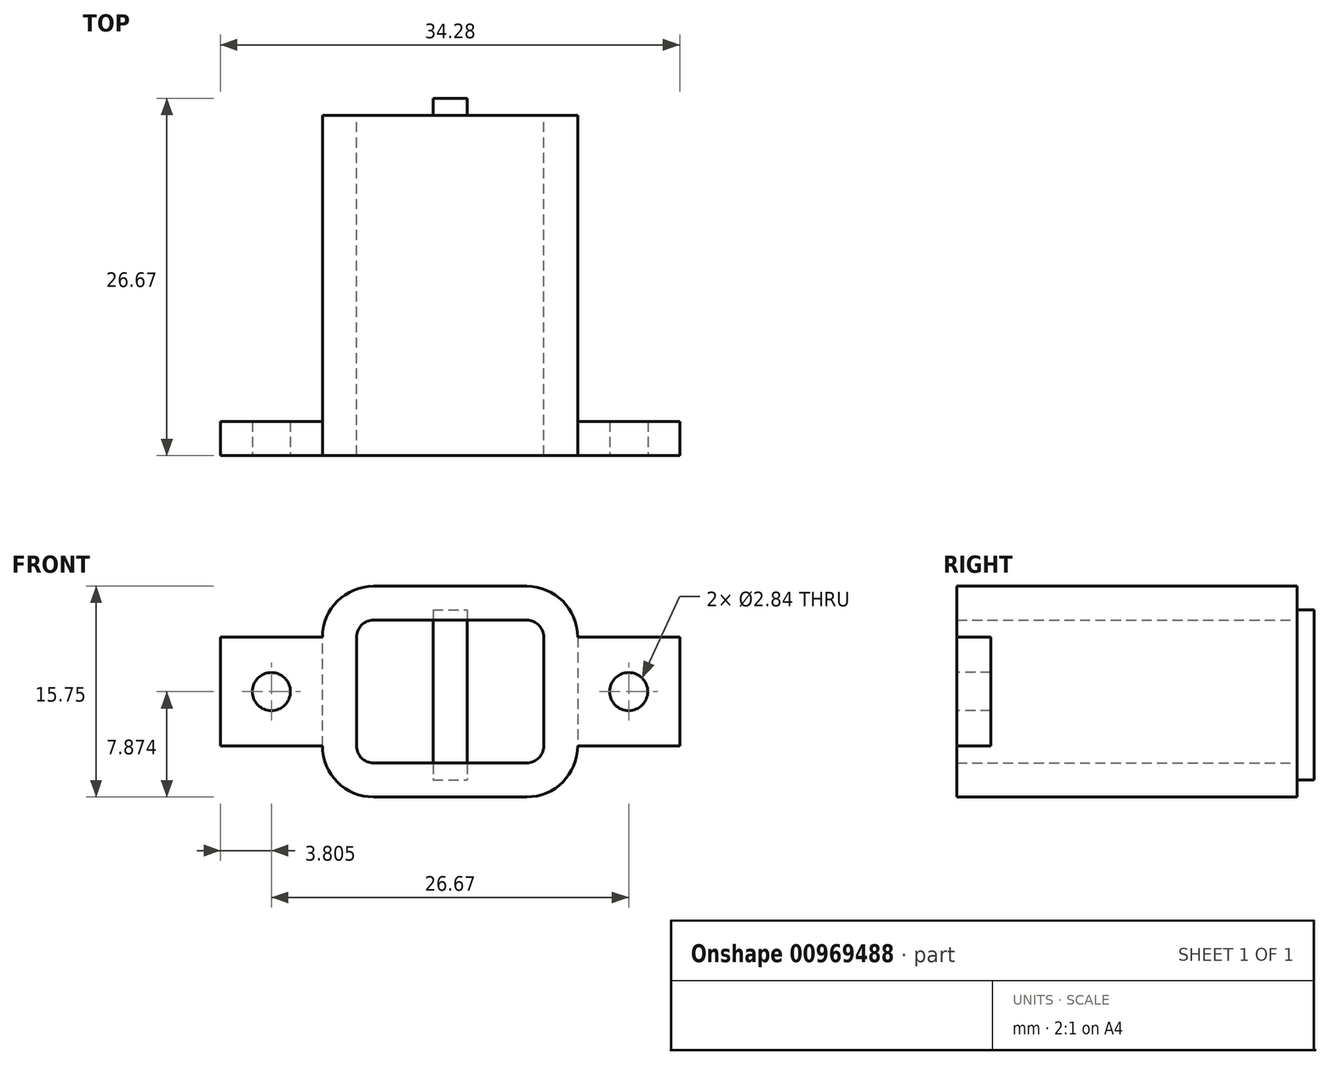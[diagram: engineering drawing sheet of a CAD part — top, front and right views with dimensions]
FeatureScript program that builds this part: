
annotation { "Feature Type Name" : "Feature", "Feature Type Description" : "" }
export const myFeature = defineFeature(function(context is Context, id is Id, definition is map)
    precondition{}
    {
        {
            var Q0;
            Q0=qCreatedBy(makeId("Front.planeOp"),FACE);
            var sketch = newSketch(context, id + "F0", { "sketchPlane" : qUnion([Q0])});
            skLineSegment(sketch, "E0", {"start": v(-6.99, 1.27) * mm, "end": v(-6.99, 9.4) * mm});
            skLineSegment(sketch, "E1", {"start": v(-5.72, 10.67) * mm, "end": v(5.72, 10.67) * mm});
            skLineSegment(sketch, "E2", {"start": v(6.99, 9.4) * mm, "end": v(6.99, 1.27) * mm});
            skPoint(sketch, "E3.visualSharp", {"position": v(-6.99, 0) * mm});
            skPoint(sketch, "E4.visualSharp", {"position": v(6.99, 0) * mm});
            skPoint(sketch, "E5.visualSharp", {"position": v(6.99, 10.67) * mm});
            skArc(sketch, "E5.filletArc", {"start": v(6.99, 9.4) * mm, "mid": v(6.61, 10.3) * mm, "end": v(5.72, 10.67) * mm});
            skPoint(sketch, "E6.visualSharp", {"position": v(-6.99, 10.67) * mm});
            skArc(sketch, "E6.filletArc", {"start": v(-5.72, 10.67) * mm, "mid": v(-6.61, 10.3) * mm, "end": v(-6.99, 9.4) * mm});
            skLineSegment(sketch, "E7", {"start": v(-5.72, 0) * mm, "end": v(5.72, 0) * mm});
            skArc(sketch, "E8.filletArc", {"start": v(-6.99, 1.27) * mm, "mid": v(-6.61, 0.37) * mm, "end": v(-5.72, 0) * mm});
            skArc(sketch, "E9.filletArc", {"start": v(5.72, 0) * mm, "mid": v(6.61, 0.37) * mm, "end": v(6.99, 1.27) * mm});
            skSolve(sketch);
        }
        {
            var Q0;
            Q0=qCreatedBy(makeId("Right.planeOp"),FACE);
            var sketch = newSketch(context, id + "F1", { "sketchPlane" : qUnion([Q0])});
            skLineSegment(sketch, "E10", {"start": v(-12.7, 13.2) * mm, "end": v(-12.7, 10.67) * mm});
            skLineSegment(sketch, "E11", {"start": v(12.7, 13.2) * mm, "end": v(12.7, 10.67) * mm});
            skLineSegment(sketch, "E12", {"start": v(12.7, 13.2) * mm, "end": v(-12.7, 13.2) * mm});
            skLineSegment(sketch, "E13", {"start": v(-12.7, 10.67) * mm, "end": v(12.7, 10.67) * mm});
            skSolve(sketch);
        }
        {
            var Q0;
            Q0 = qSketchRegion(id + "F1", true);
            var Q1;
            Q1=sQuery(id+"F0.wireOp",EDGE,"E1");
            var Q2;
            Q2=sQuery(id+"F0.wireOp",EDGE,"E6.filletArc");
            var Q3;
            Q3=sQuery(id+"F0.wireOp",EDGE,"E0");
            var Q4;
            Q4=sQuery(id+"F0.wireOp",EDGE,"E8.filletArc");
            var Q5;
            Q5=sQuery(id+"F0.wireOp",EDGE,"E7");
            var Q6;
            Q6=sQuery(id+"F0.wireOp",EDGE,"E9.filletArc");
            var Q7;
            Q7=sQuery(id+"F0.wireOp",EDGE,"E2");
            var Q8;
            Q8=sQuery(id+"F0.wireOp",EDGE,"E5.filletArc");
            sweep(context, id + "F2", {"profiles" : qUnion([Q0]), "path" : qUnion([Q1, Q2, Q3, Q4, Q5, Q6, Q7, Q8])});
        }
        {
            var Q0;
            Q0=makeQuery(id+"F2.opSweep","SWEPT_FACE",FACE,{"disambiguationData":[OSD([sQuery(id+"F0.wireOp",EDGE,"E0"),sQuery(id+"F1.wireOp",EDGE,"E12")])]});
            var sketch = newSketch(context, id + "F3", { "sketchPlane" : qUnion([Q0])});
            skLineSegment(sketch, "E14", {"start": v(12.7, 9.4) * mm, "end": v(12.7, 1.27) * mm});
            skLineSegment(sketch, "E15", {"start": v(12.7, 1.27) * mm, "end": v(10.16, 1.27) * mm});
            skLineSegment(sketch, "E16", {"start": v(10.16, 1.27) * mm, "end": v(10.16, 9.4) * mm});
            skLineSegment(sketch, "E17", {"start": v(10.16, 9.4) * mm, "end": v(12.7, 9.4) * mm});
            skSolve(sketch);
        }
        {
            var Q0;
            Q0=makeQuery(id+"F3.imprint","IMPRINT",FACE,{"disambiguationData":[TD([[makeQuery(id+"F3.imprint","IMPRINT",EDGE,{"derivedFrom":sQuery(id+"F3.wireOp",EDGE,"E14")}),1.0]])]});
            extrude(context, id + "F4", {"entities" : qUnion([Q0]), "operationType" : NewBodyOperationType.ADD, "depth" : 7.62 * mm, "offsetDistance" : 25.4 * mm});
        }
        {
            var Q0;
            Q0=makeQuery(id+"F2.opSweep","SWEPT_FACE",FACE,{"disambiguationData":[OSD([sQuery(id+"F0.wireOp",EDGE,"E2"),sQuery(id+"F1.wireOp",EDGE,"E12")])]});
            var sketch = newSketch(context, id + "F5", { "sketchPlane" : qUnion([Q0])});
            skLineSegment(sketch, "E18", {"start": v(-12.7, 1.27) * mm, "end": v(-12.7, 9.4) * mm});
            skLineSegment(sketch, "E19", {"start": v(-12.7, 9.4) * mm, "end": v(-10.16, 9.4) * mm});
            skLineSegment(sketch, "E20", {"start": v(-10.16, 9.4) * mm, "end": v(-10.16, 1.27) * mm});
            skLineSegment(sketch, "E21", {"start": v(-10.16, 1.27) * mm, "end": v(-12.7, 1.27) * mm});
            skSolve(sketch);
        }
        {
            var Q0;
            Q0=makeQuery(id+"F5.imprint","IMPRINT",FACE,{"disambiguationData":[TD([[makeQuery(id+"F5.imprint","IMPRINT",EDGE,{"derivedFrom":sQuery(id+"F5.wireOp",EDGE,"E18")}),1.0]])]});
            extrude(context, id + "F6", {"entities" : qUnion([Q0]), "operationType" : NewBodyOperationType.ADD, "depth" : 7.62 * mm, "offsetDistance" : 25.4 * mm});
        }
        {
            var Q0;
            Q0=makeQuery(id+"F6.boolean.opBoolean","MERGE",FACE,{"derivedFrom":[makeQuery(id+"F4.boolean.opBoolean","MERGE",FACE,{"derivedFrom":[makeQuery(id+"F2.opSweep","SWEPT_FACE",FACE,{"disambiguationData":[OSD([sQuery(id+"F0.wireOp",EDGE,"E1"),sQuery(id+"F1.wireOp",EDGE,"E10")])]}),makeQuery(id+"F4.opExtrude","SWEPT_FACE",FACE,{"disambiguationData":[OSD([sQuery(id+"F3.wireOp",EDGE,"E14")])]})]}),makeQuery(id+"F6.opExtrude","SWEPT_FACE",FACE,{"disambiguationData":[OSD([sQuery(id+"F5.wireOp",EDGE,"E18")])]})]});
            var sketch = newSketch(context, id + "F7", { "sketchPlane" : qUnion([Q0])});
            skLineSegment(sketch, "E22", {"start": v(-9.53, 9.4) * mm, "end": v(-9.53, 1.27) * mm, "construction": true});
            skCircle(sketch, "E23", {"center": v(-13.33, 5.33) * mm, "radius": 1.42 * mm});
            skLineSegment(sketch, "E24", {"start": v(-13.33, 5.33) * mm, "end": v(-13.34, 9.4) * mm, "construction": true});
            skLineSegment(sketch, "E25", {"start": v(-13.33, 1.27) * mm, "end": v(-13.33, 5.33) * mm, "construction": true});
            skSolve(sketch);
        }
        {
            var Q0;
            Q0 = qSketchRegion(id + "F7", true);
            extrude(context, id + "F8", {"entities" : qUnion([Q0]), "operationType" : NewBodyOperationType.REMOVE, "endBound" : BoundingType.THROUGH_ALL, "oppositeDirection" : true, "depth" : 25.4 * mm, "offsetDistance" : 25.4 * mm});
        }
        {
            var Q0;
            Q0=makeQuery(id+"F6.boolean.opBoolean","MERGE",FACE,{"derivedFrom":[makeQuery(id+"F4.boolean.opBoolean","MERGE",FACE,{"derivedFrom":[makeQuery(id+"F2.opSweep","SWEPT_FACE",FACE,{"disambiguationData":[OSD([sQuery(id+"F0.wireOp",EDGE,"E1"),sQuery(id+"F1.wireOp",EDGE,"E10")])]}),makeQuery(id+"F4.opExtrude","SWEPT_FACE",FACE,{"disambiguationData":[OSD([sQuery(id+"F3.wireOp",EDGE,"E14")])]})]}),makeQuery(id+"F6.opExtrude","SWEPT_FACE",FACE,{"disambiguationData":[OSD([sQuery(id+"F5.wireOp",EDGE,"E18")])]})]});
            var sketch = newSketch(context, id + "F9", { "sketchPlane" : qUnion([Q0])});
            skCircle(sketch, "E26", {"center": v(13.33, 5.33) * mm, "radius": 1.42 * mm});
            skLineSegment(sketch, "E27", {"start": v(13.33, 5.33) * mm, "end": v(13.34, 1.27) * mm, "construction": true});
            skLineSegment(sketch, "E28", {"start": v(13.33, 5.33) * mm, "end": v(13.33, 9.4) * mm, "construction": true});
            skSolve(sketch);
        }
        {
            var Q0;
            Q0 = qSketchRegion(id + "F9", true);
            extrude(context, id + "F10", {"entities" : qUnion([Q0]), "operationType" : NewBodyOperationType.REMOVE, "endBound" : BoundingType.THROUGH_ALL, "oppositeDirection" : true, "depth" : 25.4 * mm, "offsetDistance" : 25.4 * mm});
        }
        {
            var Q0;
            Q0=makeQuery(id+"F2.opSweep","SWEPT_FACE",FACE,{"disambiguationData":[OSD([sQuery(id+"F0.wireOp",EDGE,"E1"),sQuery(id+"F1.wireOp",EDGE,"E11")])]});
            var sketch = newSketch(context, id + "F11", { "sketchPlane" : qUnion([Q0])});
            skLineSegment(sketch, "E29", {"start": v(1.27, 11.43) * mm, "end": v(0, 11.43) * mm});
            skLineSegment(sketch, "E30", {"start": v(0, 11.43) * mm, "end": v(-1.27, 11.43) * mm});
            skLineSegment(sketch, "E31", {"start": v(-1.27, 11.43) * mm, "end": v(-1.27, -1.27) * mm});
            skLineSegment(sketch, "E32", {"start": v(1.27, 11.43) * mm, "end": v(1.27, -1.27) * mm});
            skLineSegment(sketch, "E33", {"start": v(1.27, -1.27) * mm, "end": v(-1.27, -1.27) * mm});
            skSolve(sketch);
        }
        {
            var Q0;
            Q0 = qSketchRegion(id + "F11", true);
            extrude(context, id + "F12", {"entities" : qUnion([Q0]), "operationType" : NewBodyOperationType.ADD, "depth" : 1.27 * mm, "offsetDistance" : 25.4 * mm});
        }
    });
